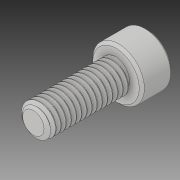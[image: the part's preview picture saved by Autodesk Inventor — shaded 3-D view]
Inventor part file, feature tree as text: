
AUTODESK INVENTOR PART (.ipt)
format: ipt  version: 2018 (Build 220112000, 112)  size: 764,928 bytes
history: native  units: in
note: dims shown in document units (in); Inventor stores cm internally (conversion verified against a paired STEP export)
features: chamfer x1
ambient origin geometry x8: Origin, YZ Plane, XZ Plane, XY Plane, X Axis, Y Axis, Z Axis, Center Point
bodies: Solid1 (feature_tree)
feature tree (1):
  chamfer  "Chamfer1"  [1 undecoded]
note: 1 required parameter value undecoded (feature->parameter linkage not recoverable at this tier; creation-order binding heuristic only, values carry confidence <= 0.55)
